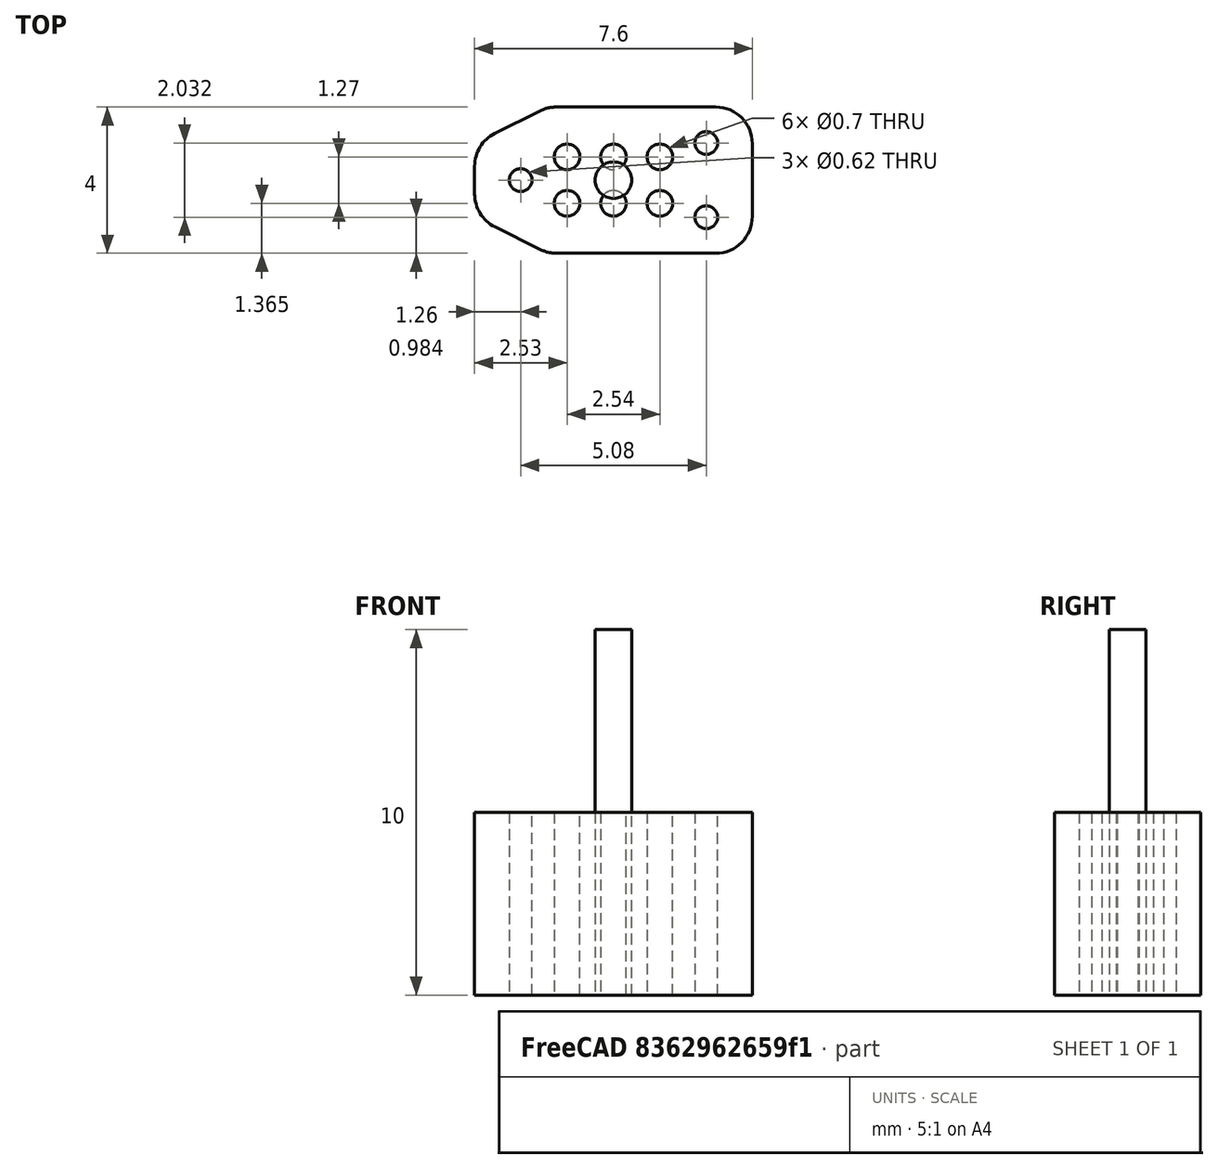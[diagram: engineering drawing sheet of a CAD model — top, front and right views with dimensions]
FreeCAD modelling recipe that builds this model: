
FCSTD DOCUMENT  (FreeCAD 0.20R29410 (Git))
Label: TC2030-NL
License: All rights reserved
LicenseURL: http://en.wikipedia.org/wiki/All_rights_reserved
objects: Part::Cylinder×10, Part::Compound×3, Part::Box×1, Part::Chamfer×1, Part::Fillet×1, Part::Cut×1
note: 17 computed .brp shape members not serialized (recipe doc carries the construction recipe); baked Part::Feature solids carry a one-line shape summary decoded from their .brp

FEATURE [Part::Box] Box  label="base"
  AttacherType = Attacher::AttachEngine3D
  Height = 5
  Length = 7.6
  Placement = pos=(-3.8,-2,0) rot=(0,0,1;0rad)
  Width = 4
  expr: .Placement.Base.x = -(Length / 2)
  expr: .Placement.Base.y = -(Width / 2)
FEATURE [Part::Cylinder] Cylinder
  Angle = 360
  AttacherType = Attacher::AttachEngine3D
  FirstAngle = 0
  Height = 10
  Radius = 0.5
  SecondAngle = 0
FEATURE [Part::Cylinder] Cylinder001  label="pin001"
  Angle = 360
  AttacherType = Attacher::AttachEngine3D
  FirstAngle = 0
  Height = 10
  Placement = pos=(0,0.635,0) rot=(0,0,1;0rad)
  Radius = 0.35
  SecondAngle = 0
FEATURE [Part::Cylinder] Cylinder002  label="pin002"
  Angle = 360
  AttacherType = Attacher::AttachEngine3D
  FirstAngle = 0
  Height = 10
  Placement = pos=(0,-0.635,0) rot=(0,0,1;0rad)
  Radius = 0.35
  SecondAngle = 0
FEATURE [Part::Cylinder] Cylinder003  label="pin003"
  Angle = 360
  AttacherType = Attacher::AttachEngine3D
  FirstAngle = 0
  Height = 10
  Placement = pos=(-1.27,0.635,0) rot=(0,0,1;0rad)
  Radius = 0.35
  SecondAngle = 0
FEATURE [Part::Cylinder] Cylinder004  label="pin004"
  Angle = 360
  AttacherType = Attacher::AttachEngine3D
  FirstAngle = 0
  Height = 10
  Placement = pos=(-1.27,-0.635,0) rot=(0,0,1;0rad)
  Radius = 0.35
  SecondAngle = 0
FEATURE [Part::Cylinder] Cylinder005  label="pin005"
  Angle = 360
  AttacherType = Attacher::AttachEngine3D
  FirstAngle = 0
  Height = 10
  Placement = pos=(1.27,0.635,0) rot=(0,0,1;0rad)
  Radius = 0.35
  SecondAngle = 0
FEATURE [Part::Cylinder] Cylinder006  label="pin006"
  Angle = 360
  AttacherType = Attacher::AttachEngine3D
  FirstAngle = 0
  Height = 10
  Placement = pos=(1.27,-0.635,0) rot=(0,0,1;0rad)
  Radius = 0.35
  SecondAngle = 0
FEATURE [Part::Cylinder] Cylinder007  label="guide1"
  Angle = 360
  AttacherType = Attacher::AttachEngine3D
  FirstAngle = 0
  Height = 10
  Placement = pos=(-2.54,0,0) rot=(0,0,1;0rad)
  Radius = 0.31
  SecondAngle = 0
FEATURE [Part::Cylinder] Cylinder008  label="guide002"
  Angle = 360
  AttacherType = Attacher::AttachEngine3D
  FirstAngle = 0
  Height = 10
  Placement = pos=(2.54,1.016,0) rot=(0,0,1;0rad)
  Radius = 0.31
  SecondAngle = 0
FEATURE [Part::Cylinder] Cylinder009  label="guide003"
  Angle = 360
  AttacherType = Attacher::AttachEngine3D
  FirstAngle = 0
  Height = 10
  Placement = pos=(2.54,-1.016,0) rot=(0,0,1;0rad)
  Radius = 0.31
  SecondAngle = 0
FEATURE [Part::Chamfer] Chamfer
  Base = -> Box
  Edges = 2 edges: [Edge1 r1=1 r2=2,Edge3 r1=1 r2=2]
FEATURE [Part::Fillet] Fillet
  Base = -> Chamfer
  Edges = 6 edges r=1: [Edge2,Edge4,Edge11,Edge13,Edge17,Edge18]
FEATURE [Part::Compound] Compound  label="Pins"
  Links = -> [Cylinder006,Cylinder001,Cylinder002,Cylinder003,Cylinder004,Cylinder005]
FEATURE [Part::Compound] Compound001  label="Guides"
  Links = -> [Cylinder007,Cylinder008,Cylinder009]
FEATURE [Part::Compound] Compound002  label="Cutouts"
  Links = -> [Compound001,Compound]
FEATURE [Part::Cut] Cut  label="TC2030-NL"
  Base = -> Fillet
  Tool = -> Compound002
